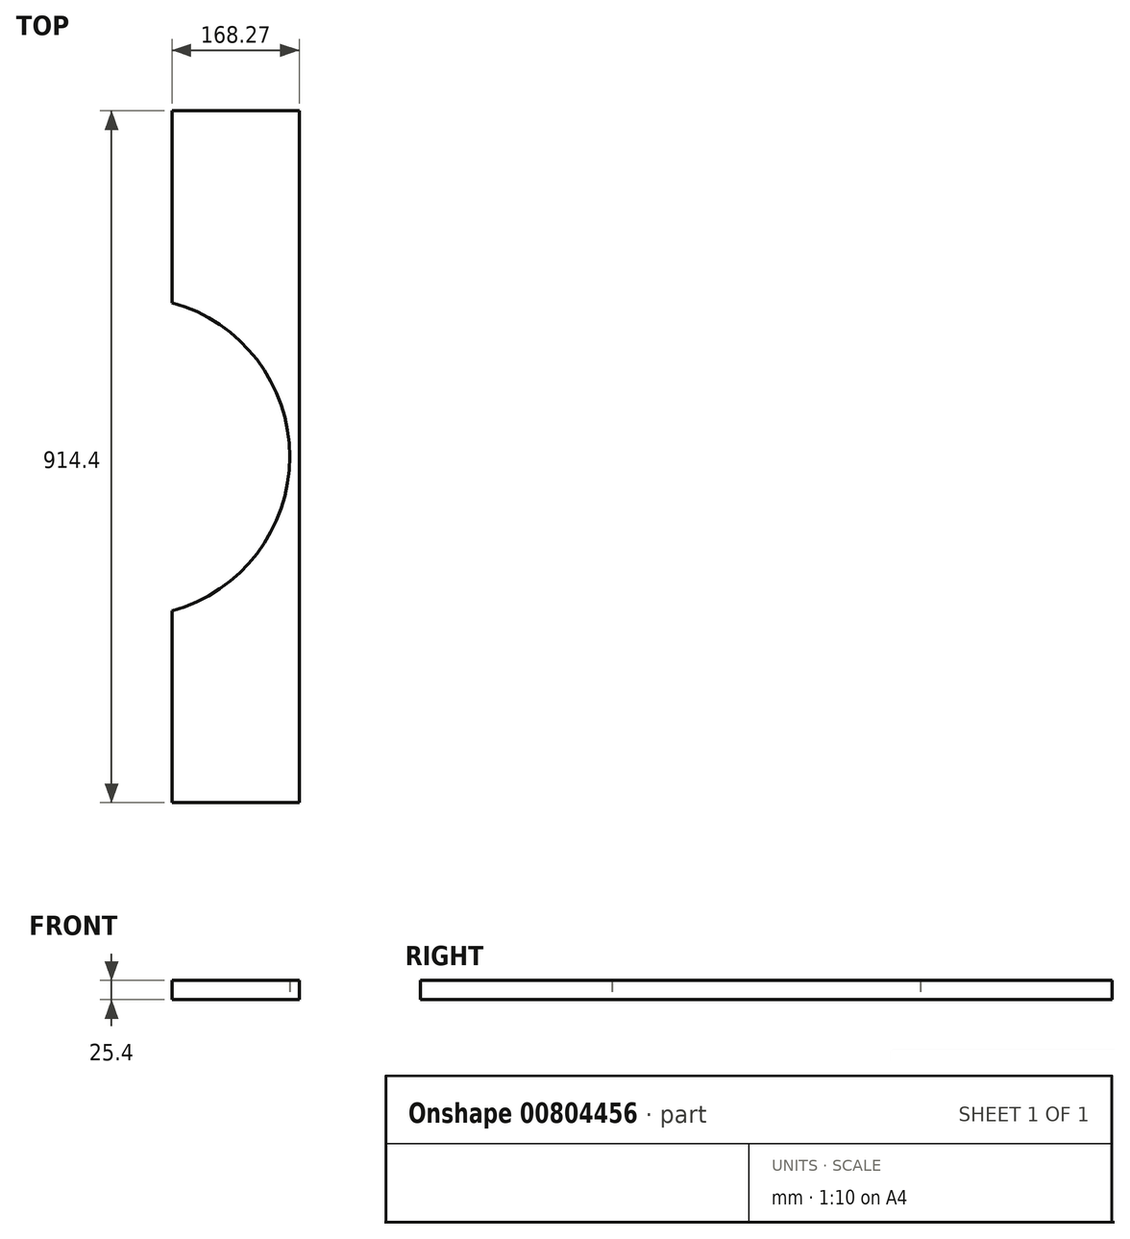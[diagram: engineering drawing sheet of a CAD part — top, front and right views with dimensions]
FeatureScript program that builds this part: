
annotation { "Feature Type Name" : "Feature", "Feature Type Description" : "" }
export const myFeature = defineFeature(function(context is Context, id is Id, definition is map)
    precondition{}
    {
        {
            var Q0;
            Q0=qCreatedBy(makeId("Top.planeOp"),FACE);
            var sketch = newSketch(context, id + "F0", { "sketchPlane" : qUnion([Q0])});
            skLineSegment(sketch, "E0.bottom", {"start": v(0, 0) * mm, "end": v(-177.8, 0) * mm});
            skLineSegment(sketch, "E0.top", {"start": v(0, 914.4) * mm, "end": v(-177.8, 914.4) * mm});
            skLineSegment(sketch, "E0.left", {"start": v(0, 0) * mm, "end": v(0, 914.4) * mm});
            skLineSegment(sketch, "E0.right", {"start": v(-177.8, 0) * mm, "end": v(-177.8, 914.4) * mm});
            skCircle(sketch, "E1", {"center": v(-233.36, 457.2) * mm, "radius": 204.79 * mm});
            skPoint(sketch, "E1.centerSnap0", {"position": v(-177.8, 457.2) * mm});
            skLineSegment(sketch, "E2", {"start": v(-9.53, 914.4) * mm, "end": v(-9.52, 0) * mm});
            skCircle(sketch, "E3.0", {"center": v(-233.36, 457.2) * mm, "radius": 211.14 * mm});
            skSolve(sketch);
        }
        {
            var Q0;
            {var subQ8=sQuery(id+"F0.wireOp",EDGE,"E2");Q0=makeQuery(id+"F0.imprint","IMPRINT",FACE,{"disambiguationData":[TD([[makeQuery(id+"F0.imprint","IMPRINT",EDGE,{"derivedFrom":subQ8}),-1.0]])]});}
            var Q1;
            {var subQ0=sQuery(id+"F0.wireOp",EDGE,"E3.0");var subQ1=sQuery(id+"F0.wireOp",EDGE,"E0.right");var subQ2=makeQuery(id+"F0.imprint","INTERSECT",VERTEX,{"disambiguationData":[OD(0.0)],"derivedFrom":[subQ1,subQ0]});Q1=makeQuery(id+"F0.imprint","IMPRINT",FACE,{"disambiguationData":[TD([[makeQuery(id+"F0.imprint","IMPRINT",EDGE,{"disambiguationData":[TD([[subQ2,-1.0]])],"derivedFrom":subQ1}),1.0]])]});}
            var Q2;
            {var subQ0=sQuery(id+"F0.wireOp",EDGE,"E3.0");var subQ1=sQuery(id+"F0.wireOp",EDGE,"E0.right");var subQ2=makeQuery(id+"F0.imprint","INTERSECT",VERTEX,{"disambiguationData":[OD(0.0)],"derivedFrom":[subQ1,subQ0]});Q2=makeQuery(id+"F0.imprint","IMPRINT",FACE,{"disambiguationData":[TD([[makeQuery(id+"F0.imprint","IMPRINT",EDGE,{"disambiguationData":[TD([[subQ2,-1.0]])],"derivedFrom":subQ1}),-1.0]])]});}
            extrude(context, id + "F1", {"entities" : qUnion([Q0, Q1, Q2]), "depth" : 25.4 * mm, "offsetDistance" : 25.4 * mm});
        }
    });
